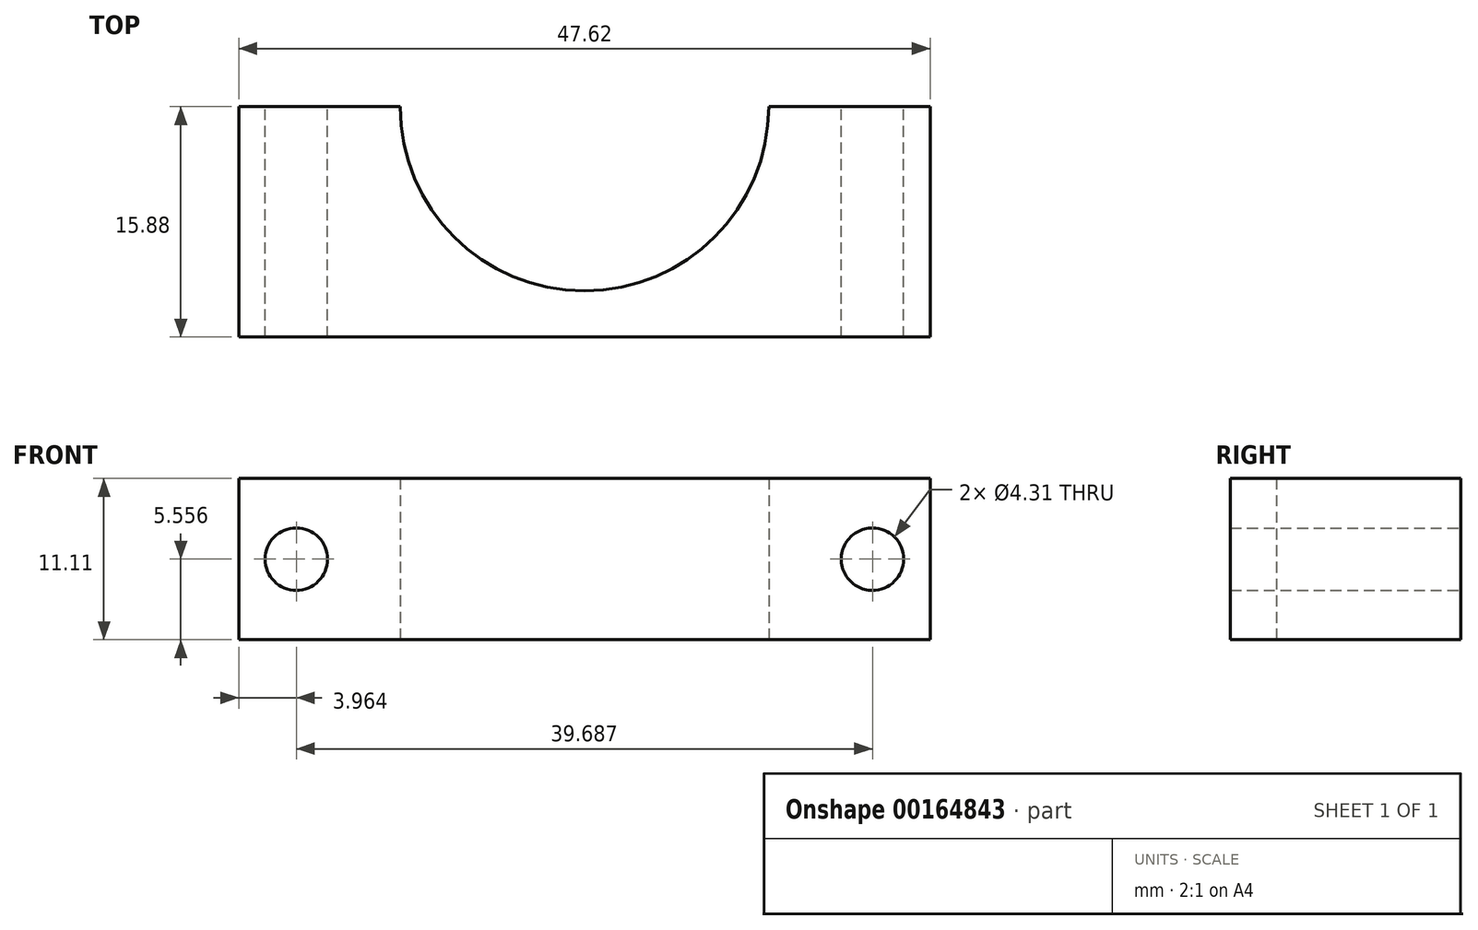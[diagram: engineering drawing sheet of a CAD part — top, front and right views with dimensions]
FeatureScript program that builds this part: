
annotation { "Feature Type Name" : "Feature", "Feature Type Description" : "" }
export const myFeature = defineFeature(function(context is Context, id is Id, definition is map)
    precondition{}
    {
        {
            var Q0;
            Q0=qCreatedBy(makeId("Top.planeOp"),FACE);
            var sketch = newSketch(context, id + "F0", { "sketchPlane" : qUnion([Q0])});
            skLineSegment(sketch, "E0.top", {"start": v(0, -15.88) * mm, "end": v(-47.62, -15.88) * mm});
            skLineSegment(sketch, "E0.left", {"start": v(0, 0) * mm, "end": v(0, -15.88) * mm});
            skLineSegment(sketch, "E0.right", {"start": v(-47.62, 0) * mm, "end": v(-47.62, -15.88) * mm});
            skLineSegment(sketch, "E1", {"start": v(-47.62, 0) * mm, "end": v(-36.51, 0) * mm});
            skLineSegment(sketch, "E2", {"start": v(-36.51, 0) * mm, "end": v(-11.11, 0) * mm, "construction": true});
            skLineSegment(sketch, "E3", {"start": v(-11.11, 0) * mm, "end": v(0, 0) * mm});
            skArc(sketch, "E4", {"start": v(-36.51, 0) * mm, "mid": v(-23.81, -12.7) * mm, "end": v(-11.11, 0) * mm});
            skSolve(sketch);
        }
        {
            var Q0;
            Q0 = qSketchRegion(id + "F0", true);
            extrude(context, id + "F1", {"entities" : qUnion([Q0]), "depth" : 11.1 * mm});
        }
        {
            var Q0;
            Q0=makeQuery(id+"F1.opExtrude","SWEPT_FACE",FACE,{"disambiguationData":[OSD([sQuery(id+"F0.wireOp",EDGE,"E1")])]});
            var sketch = newSketch(context, id + "F2", { "sketchPlane" : qUnion([Q0])});
            skLineSegment(sketch, "E5", {"start": v(47.62, 5.56) * mm, "end": v(43.66, 5.56) * mm, "construction": true});
            skLineSegment(sketch, "E6", {"start": v(0, 5.56) * mm, "end": v(3.97, 5.56) * mm, "construction": true});
            skCircle(sketch, "E7", {"center": v(43.66, 5.56) * mm, "radius": 2.15 * mm});
            skCircle(sketch, "E8", {"center": v(3.97, 5.56) * mm, "radius": 2.15 * mm});
            skSolve(sketch);
        }
        {
            var Q0;
            Q0 = qSketchRegion(id + "F2", true);
            var Q1;
            Q1=makeQuery(id+"F1.opExtrude","SWEPT_FACE",FACE,{"disambiguationData":[OSD([sQuery(id+"F0.wireOp",EDGE,"E0.top")])]});
            extrude(context, id + "F3", {"entities" : qUnion([Q0]), "operationType" : NewBodyOperationType.REMOVE, "endBound" : BoundingType.UP_TO_SURFACE, "oppositeDirection" : true, "endBoundEntityFace" : qUnion([Q1]), "depth" : 25.4 * mm});
        }
    });
